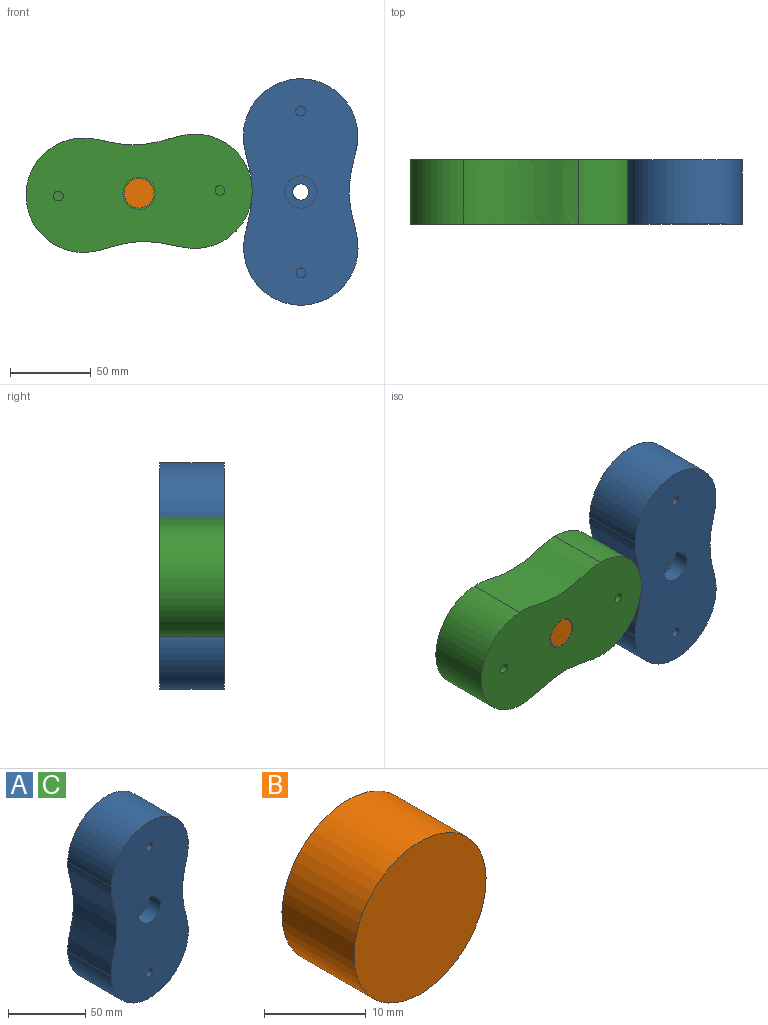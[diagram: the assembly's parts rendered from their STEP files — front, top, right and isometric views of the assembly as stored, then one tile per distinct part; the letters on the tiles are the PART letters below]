
ASSEMBLY  parts=3 mates=1
PART A: 15 faces, bbox 70.7x39.8x140 mm
  f0: cylinder r=5mm len=10mm, axis (0,-1,0), area 153.9mm2, adj f10,f13
  f1: cylinder r=35.36mm len=70.71mm, axis (0,1,0), area 4366.6mm2, adj f2,f4,f5,f6
  f2: extruded ~70.69x39.8mm, area 2854.4mm2, adj f1,f3,f5,f6
  f3: cylinder r=35.36mm len=70.71mm, axis (0,1,0), area 4365.2mm2, adj f2,f4,f5,f6
  f4: extruded ~70.68x39.8mm, area 2854.2mm2, adj f1,f3,f5,f6
  f5: plane 140.01x70.73mm, normal (0,1,0), area 7943mm2, adj f1,f2,f3,f4,f14
  f6: plane 140.01x70.73mm, normal (0,-1,0), area 8063.1mm2, adj f1,f2,f3,f4,f7,f9,f11
  f7: cylinder r=3mm len=10mm, axis (0,-1,0), area 188.5mm2, adj f6,f8
  f8: plane 6x6mm, normal (0,-1,0), area 28.3mm2, adj f7
  f9: cylinder r=10mm len=20mm, axis (0,-1,0), area 628.3mm2, adj f6,f10
  f10: plane 20x20mm, normal (0,-1,0), area 235.6mm2, adj f0,f9
  f11: cylinder r=3mm len=10mm, axis (0,-1,0), area 188.5mm2, adj f6,f12
  f12: plane 6x6mm, normal (0,-1,0), area 28.3mm2, adj f11
  f13: plane 25x25mm, normal (0,1,0), area 412.3mm2, adj f0,f14
  f14: cylinder r=12.5mm len=25mm, axis (0,1,0), area 1955.6mm2, adj f5,f13
PART B: 3 faces, bbox 18.3x10x18.3 mm
  f0: cylinder r=9.16mm len=18.31mm, axis (0,1,0), area 575.3mm2, adj f1,f2
  f1: plane 18.31x18.31mm, normal (0,-1,0), area 263.3mm2, adj f0
  f2: plane 18.31x18.31mm, normal (0,1,0), area 263.3mm2, adj f0
PART C: same geometry as A
PLACE A rot(axis=(0,-1,0),0.1deg) t=(0,39.8,0)mm
PLACE B rot(axis=(0,-1,0),0.4deg) t=(-100,10,-0.77)mm fixed
PLACE C rot(axis=(0,-1,0),92.1deg) t=(-100,39.8,-0.77)mm
MATE revolute B.f0 <-> C.f0  axis (0,-1,0) through (-100,0,-0.77)mm
